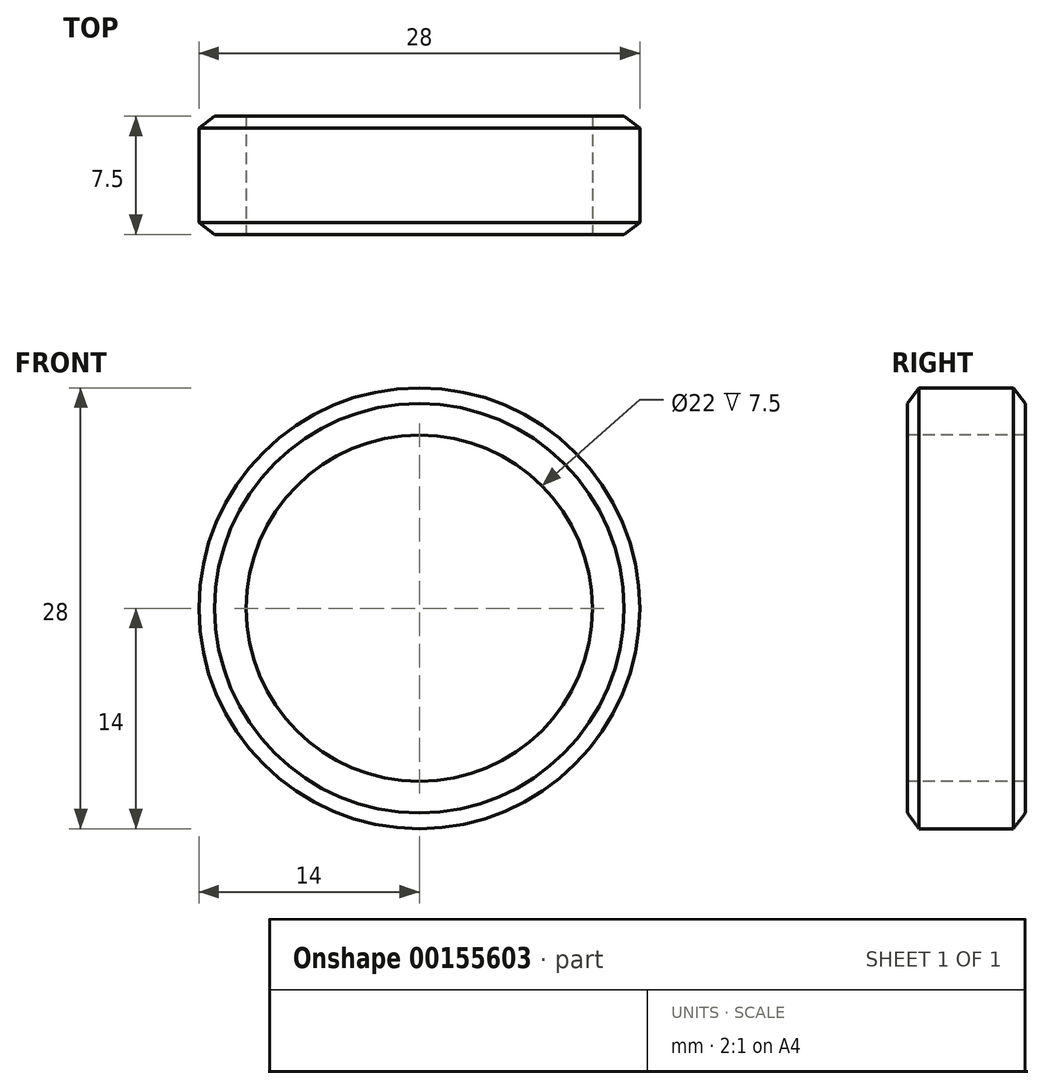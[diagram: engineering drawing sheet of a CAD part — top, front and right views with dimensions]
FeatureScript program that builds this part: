
annotation { "Feature Type Name" : "Feature", "Feature Type Description" : "" }
export const myFeature = defineFeature(function(context is Context, id is Id, definition is map)
    precondition{}
    {
        {
            var Q0;
            Q0=qCreatedBy(makeId("Top.planeOp"),FACE);
            var sketch = newSketch(context, id + "F0", { "sketchPlane" : qUnion([Q0])});
            skLineSegment(sketch, "E0.bottom", {"start": v(0, 0) * mm, "end": v(11, 0) * mm});
            skLineSegment(sketch, "E0.top", {"start": v(0, 7.5) * mm, "end": v(11, 7.5) * mm});
            skLineSegment(sketch, "E0.left", {"start": v(0, 0) * mm, "end": v(0, 7.5) * mm});
            skLineSegment(sketch, "E0.right", {"start": v(11, 0) * mm, "end": v(11, 7.5) * mm});
            skLineSegment(sketch, "E1", {"start": v(11, 7.5) * mm, "end": v(25.6, 7.5) * mm});
            skLineSegment(sketch, "E2", {"start": v(13, 7.5) * mm, "end": v(13, -3.74) * mm});
            skLineSegment(sketch, "E3", {"start": v(14, 7.5) * mm, "end": v(14, -5.88) * mm});
            skLineSegment(sketch, "E4", {"start": v(13, 7.5) * mm, "end": v(14, 6.75) * mm});
            skLineSegment(sketch, "E5", {"start": v(11, 0) * mm, "end": v(21.75, 0) * mm});
            skLineSegment(sketch, "E6", {"start": v(13, 0) * mm, "end": v(14, 0.75) * mm});
            skLineSegment(sketch, "E7", {"start": v(0, 0) * mm, "end": v(0, 14.26) * mm, "construction": true});
            skSolve(sketch);
        }
        {
            var Q0;
            {var subQ0=sQuery(id+"F0.wireOp",EDGE,"E4");Q0=makeQuery(id+"F0.imprint","IMPRINT",FACE,{"disambiguationData":[TD([[makeQuery(id+"F0.imprint","IMPRINT",EDGE,{"derivedFrom":subQ0}),-1.0]])]});}
            var Q1;
            {var subQ0=sQuery(id+"F0.wireOp",EDGE,"E0.right");Q1=makeQuery(id+"F0.imprint","IMPRINT",FACE,{"disambiguationData":[TD([[makeQuery(id+"F0.imprint","IMPRINT",EDGE,{"derivedFrom":subQ0}),-1.0]])]});}
            var Q2;
            Q2=sQuery(id+"F0.wireOp",EDGE,"E7");
            revolve(context, id + "F1", {"entities" : qUnion([Q0, Q1]), "axis" : qUnion([Q2]), "revolveType" : RevolveType.FULL});
        }
    });
